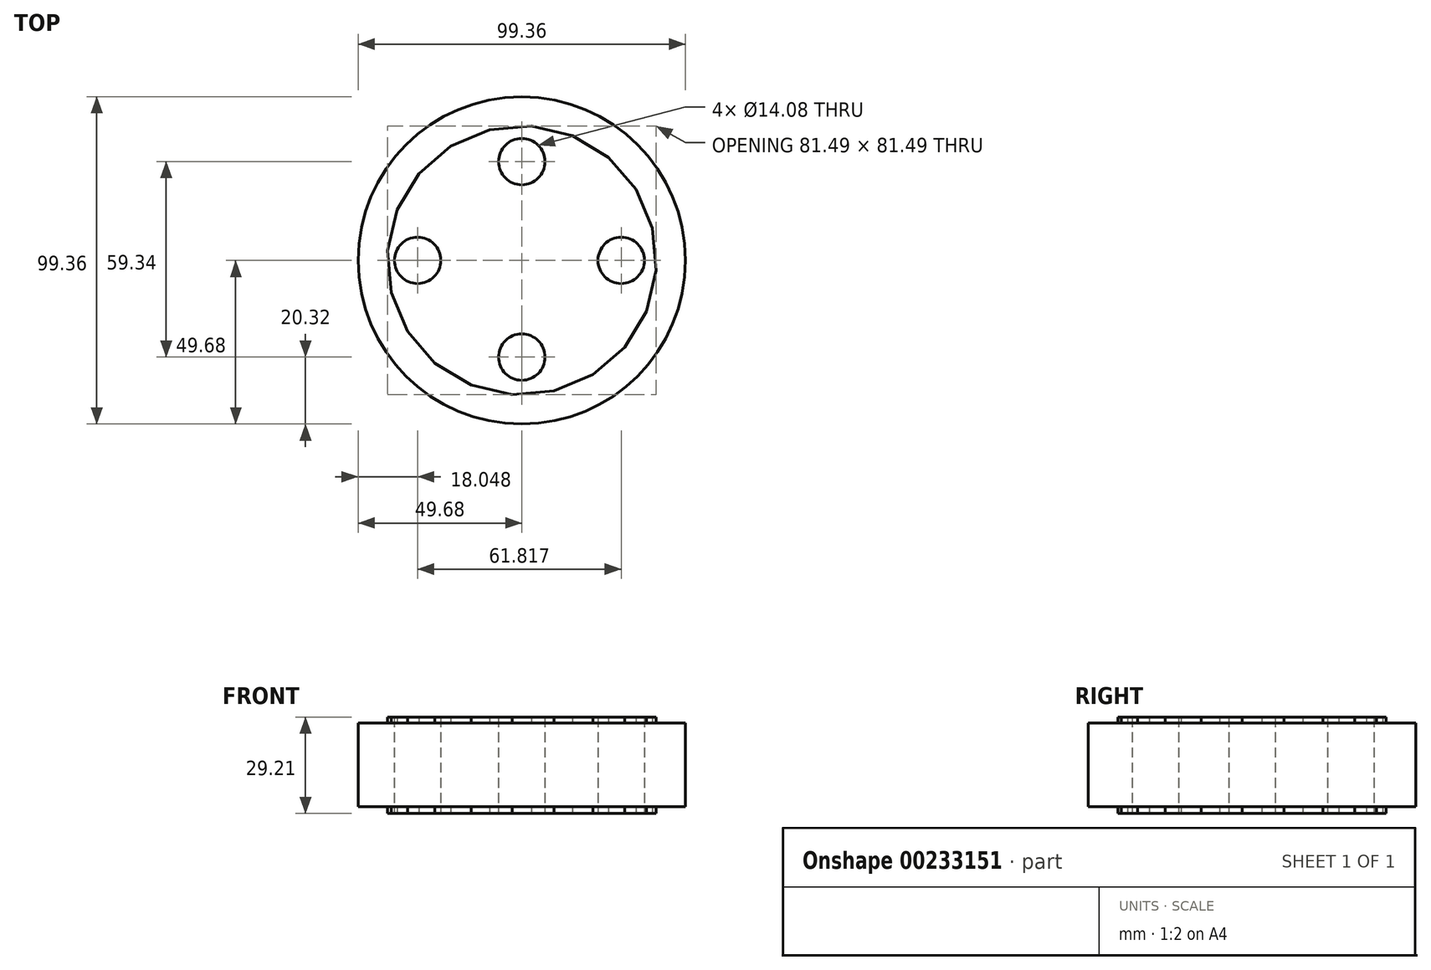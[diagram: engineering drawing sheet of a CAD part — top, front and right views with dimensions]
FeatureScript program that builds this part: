
annotation { "Feature Type Name" : "Feature", "Feature Type Description" : "" }
export const myFeature = defineFeature(function(context is Context, id is Id, definition is map)
    precondition{}
    {
        {
            var Q0;
            Q0=qCreatedBy(makeId("Top.planeOp"),FACE);
            var sketch = newSketch(context, id + "F0", { "sketchPlane" : qUnion([Q0])});
            skCircle(sketch, "E0", {"center": v(0, 29.98) * mm, "radius": 7.04 * mm});
            skCircle(sketch, "E1", {"center": v(30.18, 0) * mm, "radius": 7.04 * mm});
            skCircle(sketch, "E2", {"center": v(0, -29.36) * mm, "radius": 7.04 * mm});
            skCircle(sketch, "E3", {"center": v(-31.63, 0) * mm, "radius": 7.04 * mm});
            skSolve(sketch);
        }
        {
            var Q0;
            Q0=qCreatedBy(makeId("Top.planeOp"),FACE);
            var sketch = newSketch(context, id + "F1", { "sketchPlane" : qUnion([Q0])});
            skCircle(sketch, "E4", {"center": v(0, 0) * mm, "radius": 49.68 * mm});
            skSolve(sketch);
        }
        {
            var Q0;
            Q0=qCreatedBy(makeId("Top.planeOp"),FACE);
            var sketch = newSketch(context, id + "F2", { "sketchPlane" : qUnion([Q0])});
            skCircle(sketch, "E5.cCircle", {"center": v(0, 0) * mm, "radius": 40.35 * mm, "construction": true});
            skLineSegment(sketch, "E5.0", {"start": v(-37.83, 15.41) * mm, "end": v(-31.22, 26.35) * mm});
            skLineSegment(sketch, "E5.1", {"start": v(-31.22, 26.35) * mm, "end": v(-21.55, 34.7) * mm});
            skLineSegment(sketch, "E5.2", {"start": v(-21.55, 34.7) * mm, "end": v(-9.77, 39.67) * mm});
            skLineSegment(sketch, "E5.3", {"start": v(-9.77, 39.67) * mm, "end": v(2.97, 40.74) * mm});
            skLineSegment(sketch, "E5.4", {"start": v(2.97, 40.74) * mm, "end": v(15.41, 37.83) * mm});
            skLineSegment(sketch, "E5.5", {"start": v(15.41, 37.83) * mm, "end": v(26.35, 31.22) * mm});
            skLineSegment(sketch, "E5.6", {"start": v(26.35, 31.22) * mm, "end": v(34.7, 21.55) * mm});
            skLineSegment(sketch, "E5.7", {"start": v(34.7, 21.55) * mm, "end": v(39.67, 9.77) * mm});
            skLineSegment(sketch, "E5.8", {"start": v(39.67, 9.77) * mm, "end": v(40.74, -2.97) * mm});
            skLineSegment(sketch, "E5.9", {"start": v(40.74, -2.97) * mm, "end": v(37.83, -15.41) * mm});
            skLineSegment(sketch, "E5.10", {"start": v(37.83, -15.41) * mm, "end": v(31.22, -26.35) * mm});
            skLineSegment(sketch, "E5.11", {"start": v(31.22, -26.35) * mm, "end": v(21.55, -34.7) * mm});
            skLineSegment(sketch, "E5.12", {"start": v(21.55, -34.7) * mm, "end": v(9.77, -39.67) * mm});
            skLineSegment(sketch, "E5.13", {"start": v(9.77, -39.67) * mm, "end": v(-2.97, -40.74) * mm});
            skLineSegment(sketch, "E5.14", {"start": v(-2.97, -40.74) * mm, "end": v(-15.41, -37.83) * mm});
            skLineSegment(sketch, "E5.15", {"start": v(-15.41, -37.83) * mm, "end": v(-26.35, -31.22) * mm});
            skLineSegment(sketch, "E5.16", {"start": v(-26.35, -31.22) * mm, "end": v(-34.7, -21.55) * mm});
            skLineSegment(sketch, "E5.17", {"start": v(-34.7, -21.55) * mm, "end": v(-39.67, -9.77) * mm});
            skLineSegment(sketch, "E5.18", {"start": v(-39.67, -9.77) * mm, "end": v(-40.74, 2.97) * mm});
            skLineSegment(sketch, "E5.19", {"start": v(-40.74, 2.97) * mm, "end": v(-37.83, 15.41) * mm});
            skPoint(sketch, "E5.0.midPoint", {"position": v(-34.53, 20.88) * mm});
            skSolve(sketch);
        }
        {
            var Q0;
            Q0 = qSketchRegion(id + "F1", true);
            extrude(context, id + "F3", {"entities" : qUnion([Q0]), "depth" : 25.4 * mm});
        }
        {
            var Q0;
            Q0 = qSketchRegion(id + "F2", true);
            extrude(context, id + "F4", {"entities" : qUnion([Q0]), "operationType" : NewBodyOperationType.ADD, "depth" : 27.18 * mm, "hasSecondDirection" : true, "secondDirectionOppositeDirection" : true, "secondDirectionDepth" : 2.03 * mm});
        }
        {
            var Q0;
            Q0 = qSketchRegion(id + "F0", true);
            extrude(context, id + "F5", {"entities" : qUnion([Q0]), "operationType" : NewBodyOperationType.REMOVE, "depth" : 75.18 * mm, "hasSecondDirection" : true, "secondDirectionOppositeDirection" : true, "secondDirectionDepth" : 119.13 * mm});
        }
    });
